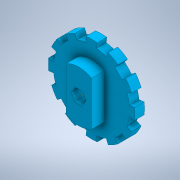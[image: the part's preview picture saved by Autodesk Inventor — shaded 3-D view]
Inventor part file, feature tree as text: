
AUTODESK INVENTOR PART (.ipt)
format: ipt  version: 2021.2 (Build 252289000, 289)  size: 217,600 bytes
history: native  units: in
note: dims shown in document units (in); Inventor stores cm internally (conversion verified against a paired STEP export)
features: extrude x5, sketch x5, pattern_circular x1
ambient origin geometry x8: Origin, YZ Plane, XZ Plane, XY Plane, X Axis, Y Axis, Z Axis, Center Point
bodies: Solid1 (feature_tree)
feature tree (11):
  extrude  "Extrusion1"  Depth=0.375in TaperAngle=0.0deg
  extrude  "Extrusion9"  TaperAngle=15.0deg  [1 undecoded]
  pattern_circular  "Circular Pattern4"  Count=12  [1 undecoded]
  extrude  "Extrusion11"  Depth=0.5in
  extrude  "Extrusion12"  TaperAngle=0.0deg  [1 undecoded]
  extrude  "Extrusion14"  Depth=0.5in
  sketch  "Sketch1"  dims[d0=3.0in d1=0.375in d2=0.0in]
  sketch  "Sketch8"  dims[d40=0.1963in d41=15.0deg]
  sketch  "Sketch10"  dims[d42=0.0515in]
  sketch  "Sketch11"  dims[d43=0.375in d44=0.0in d45=4.7244in]
  sketch  "Sketch12"  dims[d46=360.0deg d55=0.5in d56=0.0in d57=0.0in d58=2.0in d59=0.1875in d60=0.0in d61=0.5in d65=1.0in d66=0.5in d67=0.0in]
note: 3 required parameter values undecoded (feature->parameter linkage not recoverable at this tier; creation-order binding heuristic only, values carry confidence <= 0.55)
